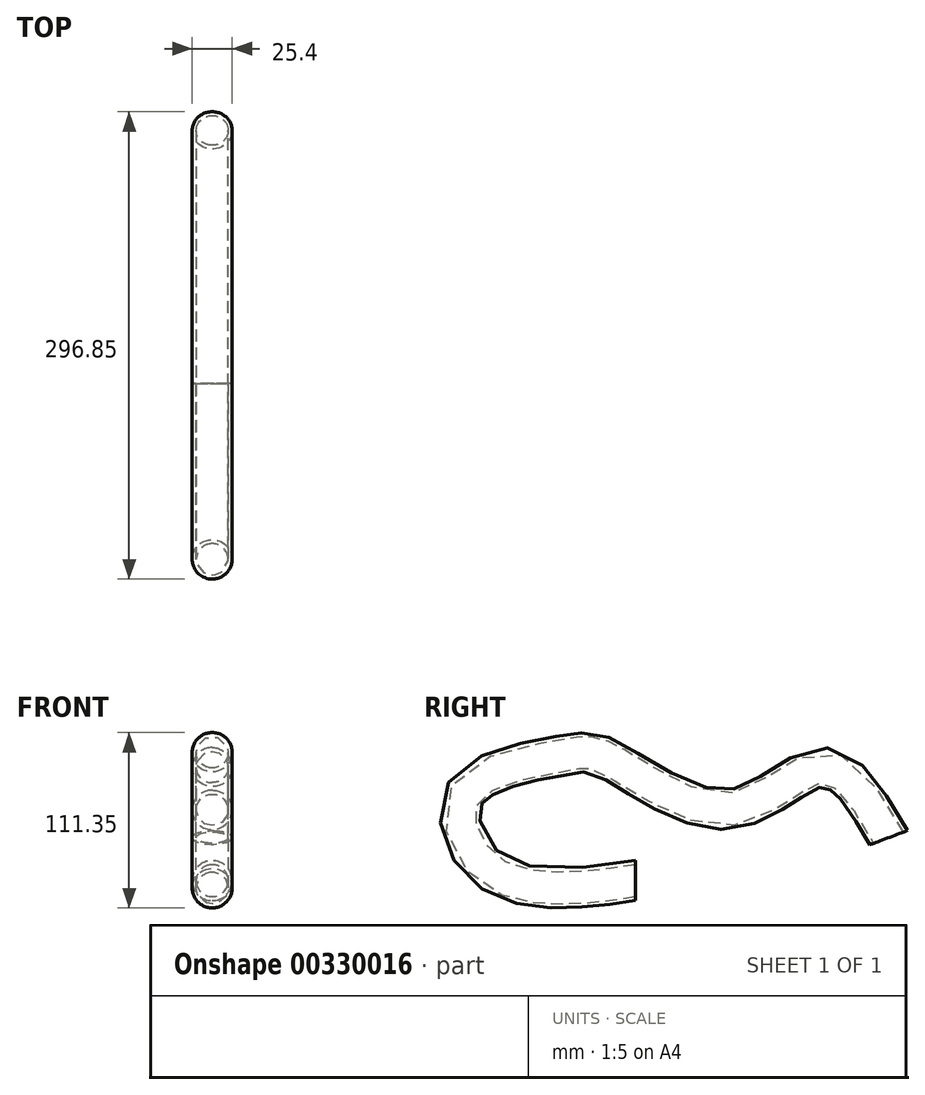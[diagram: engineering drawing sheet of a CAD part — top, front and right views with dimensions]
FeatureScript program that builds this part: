
annotation { "Feature Type Name" : "Feature", "Feature Type Description" : "" }
export const myFeature = defineFeature(function(context is Context, id is Id, definition is map)
    precondition{}
    {
        {
            var Q0;
            Q0=qCreatedBy(makeId("Front.planeOp"),FACE);
            var sketch = newSketch(context, id + "F0", { "sketchPlane" : qUnion([Q0])});
            skCircle(sketch, "E0", {"center": v(0, 76.11) * mm, "radius": 12.7 * mm});
            skSolve(sketch);
        }
        {
            var Q0;
            Q0=qCreatedBy(makeId("Right.planeOp"),FACE);
            var sketch = newSketch(context, id + "F1", { "sketchPlane" : qUnion([Q0])});
            skFitSpline(sketch, "E1", {"points": [v(0, 76.21) * mm, v(-42.2, 71.55) * mm, v(-95.55, 85.27) * mm, v(-107.45, 132.14) * mm, v(-45.26, 155.62) * mm, v(-19.73, 154.54) * mm, v(58.5, 121.1) * mm, v(119.31, 147.92) * mm, v(160.73, 103.37) * mm], "startDerivative": vector(-361.43, -57.32) * mm, "endDerivative": vector(291.45, -509.98) * mm});
            skSolve(sketch);
        }
        {
            var Q0;
            Q0=makeQuery(id+"F0.imprint","IMPRINT",FACE,{"disambiguationData":[TD([[makeQuery(id+"F0.imprint","IMPRINT",EDGE,{"derivedFrom":sQuery(id+"F0.wireOp",EDGE,"E0")}),1.0]])]});
            var Q1;
            Q1=sQuery(id+"F1.wireOp",EDGE,"E1");
            sweep(context, id + "F2", {"profiles" : qUnion([Q0]), "path" : qUnion([Q1])});
        }
        {
            var Q0;
            Q0=makeQuery(id+"F2.opSweep","CAP_FACE",FACE,{"disambiguationData":[OSD([sQuery(id+"F0.wireOp",EDGE,"E0"),sQuery(id+"F1.wireOp",VERTEX,"E1.start")])],"isStart":true});
            var Q1;
            Q1=makeQuery(id+"F2.opSweep","CAP_FACE",FACE,{"disambiguationData":[OSD([sQuery(id+"F0.wireOp",EDGE,"E0"),sQuery(id+"F1.wireOp",VERTEX,"E1.end")])],"isStart":false});
            shell(context, id + "F3", {"entities" : qUnion([Q0, Q1]), "thickness" : 2.54 * mm});
        }
    });
